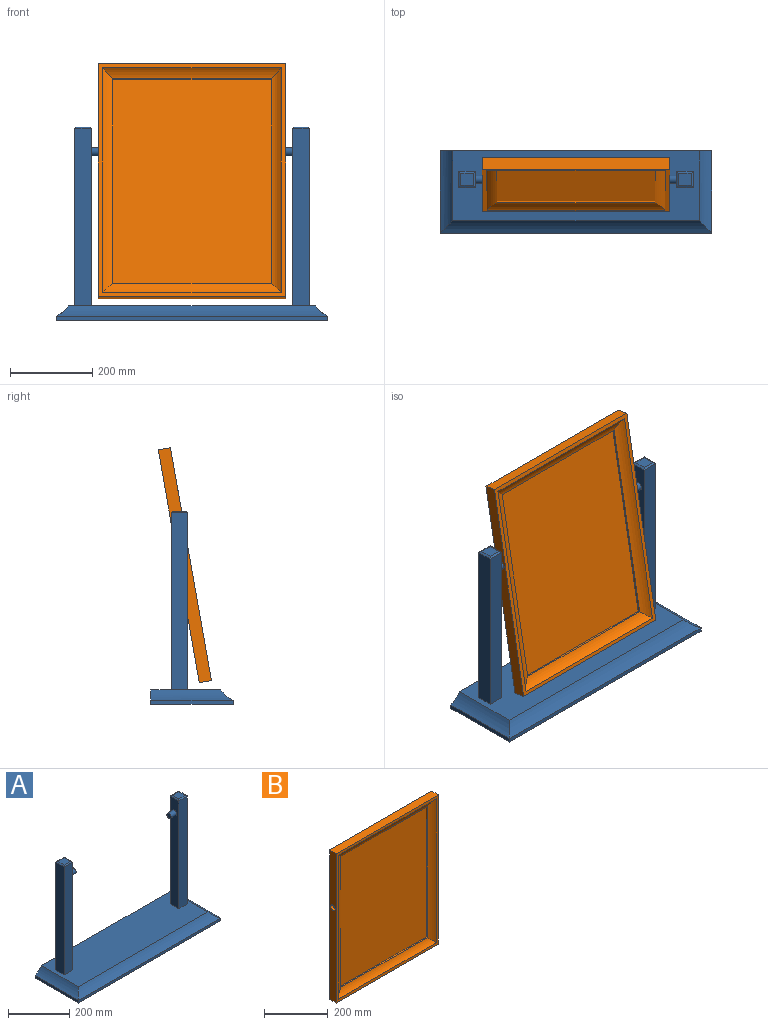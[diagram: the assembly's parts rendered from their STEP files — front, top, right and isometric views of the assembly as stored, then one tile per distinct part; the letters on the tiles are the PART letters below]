
ASSEMBLY  parts=2 mates=1
PART A: 31 faces, bbox 660x200x470 mm
  f0: plane 600x170mm, normal (0,0,1), area 98800mm2, adj f1,f2,f7,f8,f9,f10,f11,f12
  f1: plane 660x35mm, normal (0,1,0), area 22214.9mm2, adj f0,f3,f5,f6,f7,f8
  f2: cylinder r=75mm len=660mm, axis (-1,0,0), area 24801.9mm2, adj f0,f4,f7,f8
  f3: plane 660x200mm, normal (0,0,-1), area 132000mm2, adj f1,f4,f5,f6
  f4: plane 660x10mm, normal (0,-1,0), area 6600mm2, adj f2,f3,f5,f6
  f5: plane 200x10mm, normal (1,0,0), area 2000mm2, adj f1,f3,f4,f8
  f6: plane 200x10mm, normal (-1,0,0), area 2000mm2, adj f1,f3,f4,f7
  f7: cylinder r=75mm len=200mm, axis (0,1,0), area 7265.1mm2, adj f0,f1,f2,f6
  f8: cylinder r=75mm len=200mm, axis (0,1,0), area 7265.1mm2, adj f0,f1,f2,f5
  f9: plane 432x40mm, normal (1,0,0), area 17280mm2, adj f0,f10,f12,f14
  f10: plane 432x40mm, normal (0,1,0), area 17280mm2, adj f0,f9,f11,f15
  f11: plane 432x40mm, normal (-1,0,0), area 16965.8mm2, adj f0,f10,f12,f17,f18
  f12: plane 432x40mm, normal (0,-1,0), area 17280mm2, adj f0,f9,f11,f16
  f13: plane 29.61x29.61mm, normal (0,0,1), area 876.6mm2, adj f14,f15,f16,f17
  f14: plane 40x5.2mm, normal (0.5,0,0.87), area 208.8mm2, adj f9,f13,f15,f16
  f15: plane 40x5.2mm, normal (0,0.5,0.87), area 208.8mm2, adj f10,f13,f14,f17
  f16: plane 40x5.2mm, normal (0,-0.5,0.87), area 208.8mm2, adj f12,f13,f14,f17
  f17: plane 40x5.2mm, normal (-0.5,0,0.87), area 208.8mm2, adj f11,f13,f15,f16
  f18: cylinder r=10mm len=25mm, axis (1,0,0), area 1570.8mm2, adj f11,f19
  f19: plane 20x20mm, normal (-1,0,0), area 314.2mm2, adj f18
  f20: plane 432x40mm, normal (-1,0,0), area 17280mm2, adj f0,f21,f23,f25
  f21: plane 432x40mm, normal (0,1,0), area 17280mm2, adj f0,f20,f22,f26
  f22: plane 432x40mm, normal (1,0,0), area 16965.8mm2, adj f0,f21,f23,f28,f29
  f23: plane 432x40mm, normal (0,-1,0), area 17280mm2, adj f0,f20,f22,f27
  f24: plane 29.61x29.61mm, normal (0,0,1), area 876.6mm2, adj f25,f26,f27,f28
  f25: plane 40x5.2mm, normal (-0.5,0,0.87), area 208.8mm2, adj f20,f24,f26,f27
  f26: plane 40x5.2mm, normal (0,0.5,0.87), area 208.8mm2, adj f21,f24,f25,f28
  f27: plane 40x5.2mm, normal (0,-0.5,0.87), area 208.8mm2, adj f23,f24,f25,f28
  f28: plane 40x5.2mm, normal (0.5,0,0.87), area 208.8mm2, adj f22,f24,f26,f27
  f29: cylinder r=10mm len=25mm, axis (-1,0,0), area 1570.8mm2, adj f22,f30
  f30: plane 20x20mm, normal (1,0,0), area 314.2mm2, adj f29
PART B: 19 faces, bbox 455x30x575 mm
  f0: plane 505x385mm, normal (0,-1,0), area 194425mm2, adj f1,f7,f10,f12
  f1: plane 385x5mm, normal (0,0,-1), area 1925mm2, adj f0,f5,f7,f10
  f2: plane 575x455mm, normal (0,1,0), area 261625mm2, adj f3,f6,f9,f13
  f3: plane 455x30mm, normal (0,0,1), area 13650mm2, adj f2,f4,f6,f9
  f4: plane 575x455mm, normal (0,-1,0), area 20200mm2, adj f3,f5,f6,f8,f9,f11,f13,f14
  f5: cylinder r=50mm len=435mm, axis (-1,0,0), area 12173.6mm2, adj f1,f4,f8,f11
  f6: plane 575x30mm, normal (1,0,0), area 16935.8mm2, adj f2,f3,f4,f13,f17
  f7: plane 505x5mm, normal (-1,0,0), area 2525mm2, adj f0,f1,f8,f12
  f8: cylinder r=50mm len=555mm, axis (0,0,-1), area 15723.8mm2, adj f4,f5,f7,f14
  f9: plane 575x30mm, normal (-1,0,0), area 16935.8mm2, adj f2,f3,f4,f13,f15
  f10: plane 505x5mm, normal (1,0,0), area 2525mm2, adj f0,f1,f11,f12
  f11: cylinder r=50mm len=555mm, axis (0,0,-1), area 15723.8mm2, adj f4,f5,f10,f14
  f12: plane 385x5mm, normal (0,0,1), area 1925mm2, adj f0,f7,f10,f14
  f13: plane 455x30mm, normal (0,0,-1), area 13650mm2, adj f2,f4,f6,f9
  f14: cylinder r=50mm len=435mm, axis (-1,0,0), area 12173.6mm2, adj f4,f8,f11,f12
  f15: cylinder r=10mm len=20mm, axis (-1,0,0), area 628.3mm2, adj f9,f16
  f16: plane 20x20mm, normal (-1,0,0), area 314.2mm2, adj f15
  f17: cylinder r=10mm len=20mm, axis (1,0,0), area 628.3mm2, adj f6,f18
  f18: plane 20x20mm, normal (1,0,0), area 314.2mm2, adj f17
PLACE A at identity fixed
PLACE B rot(axis=(-1,0,0),10deg) t=(0,-67.82,336)mm
MATE revolute A.f18 <-> B.f15  axis (-1,0,0) through (245,-70,410)mm
